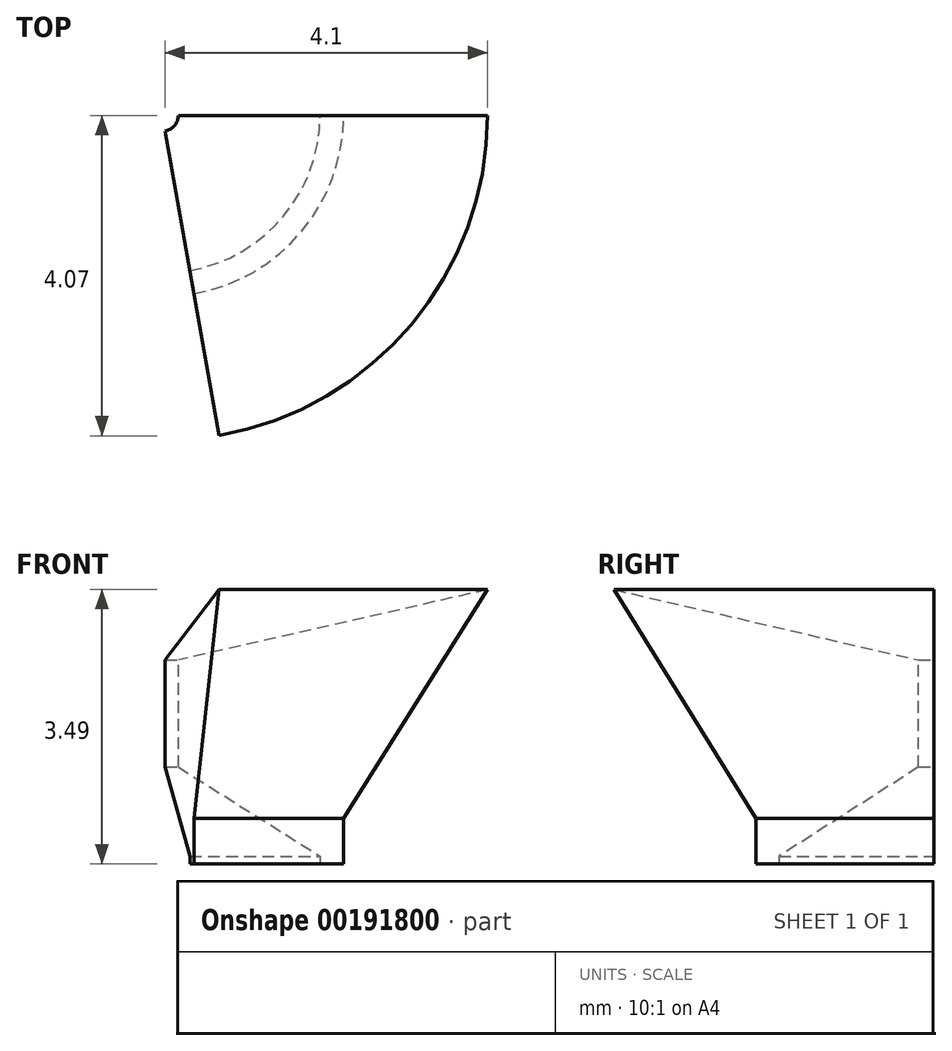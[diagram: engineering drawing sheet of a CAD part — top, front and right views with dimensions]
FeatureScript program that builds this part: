
annotation { "Feature Type Name" : "Feature", "Feature Type Description" : "" }
export const myFeature = defineFeature(function(context is Context, id is Id, definition is map)
    precondition{}
    {
        {
            var Q0;
            Q0=qCreatedBy(makeId("Front.planeOp"),FACE);
            var sketch = newSketch(context, id + "F0", { "sketchPlane" : qUnion([Q0])});
            skLineSegment(sketch, "E0", {"start": v(2, 0.1) * mm, "end": v(4.13, 3.49) * mm});
            skLineSegment(sketch, "E1", {"start": v(4.13, 3.49) * mm, "end": v(0.2, 2.6) * mm});
            skLineSegment(sketch, "E2", {"start": v(0.2, 1.23) * mm, "end": v(2, 0.1) * mm});
            skLineSegment(sketch, "E3", {"start": v(0.2, 1.23) * mm, "end": v(0.2, 2.6) * mm});
            skLineSegment(sketch, "E4", {"start": v(2, 0.1) * mm, "end": v(2, 0) * mm});
            skLineSegment(sketch, "E5", {"start": v(2.3, 0) * mm, "end": v(2.3, 0.58) * mm});
            skLineSegment(sketch, "E6", {"start": v(2, 0) * mm, "end": v(2.3, 0) * mm});
            skLineSegment(sketch, "E7", {"start": v(0, 0) * mm, "end": v(0, -2) * mm});
            skSolve(sketch);
        }
        {
            var Q0;
            Q0 = qSketchRegion(id + "F0", true);
            var Q1;
            Q1=sQuery(id+"F0.wireOp",EDGE,"E7");
            revolve(context, id + "F1", {"entities" : qUnion([Q0]), "axis" : qUnion([Q1]), "revolveType" : RevolveType.ONE_DIRECTION, "angle" : 80 * degree});
        }
    });
